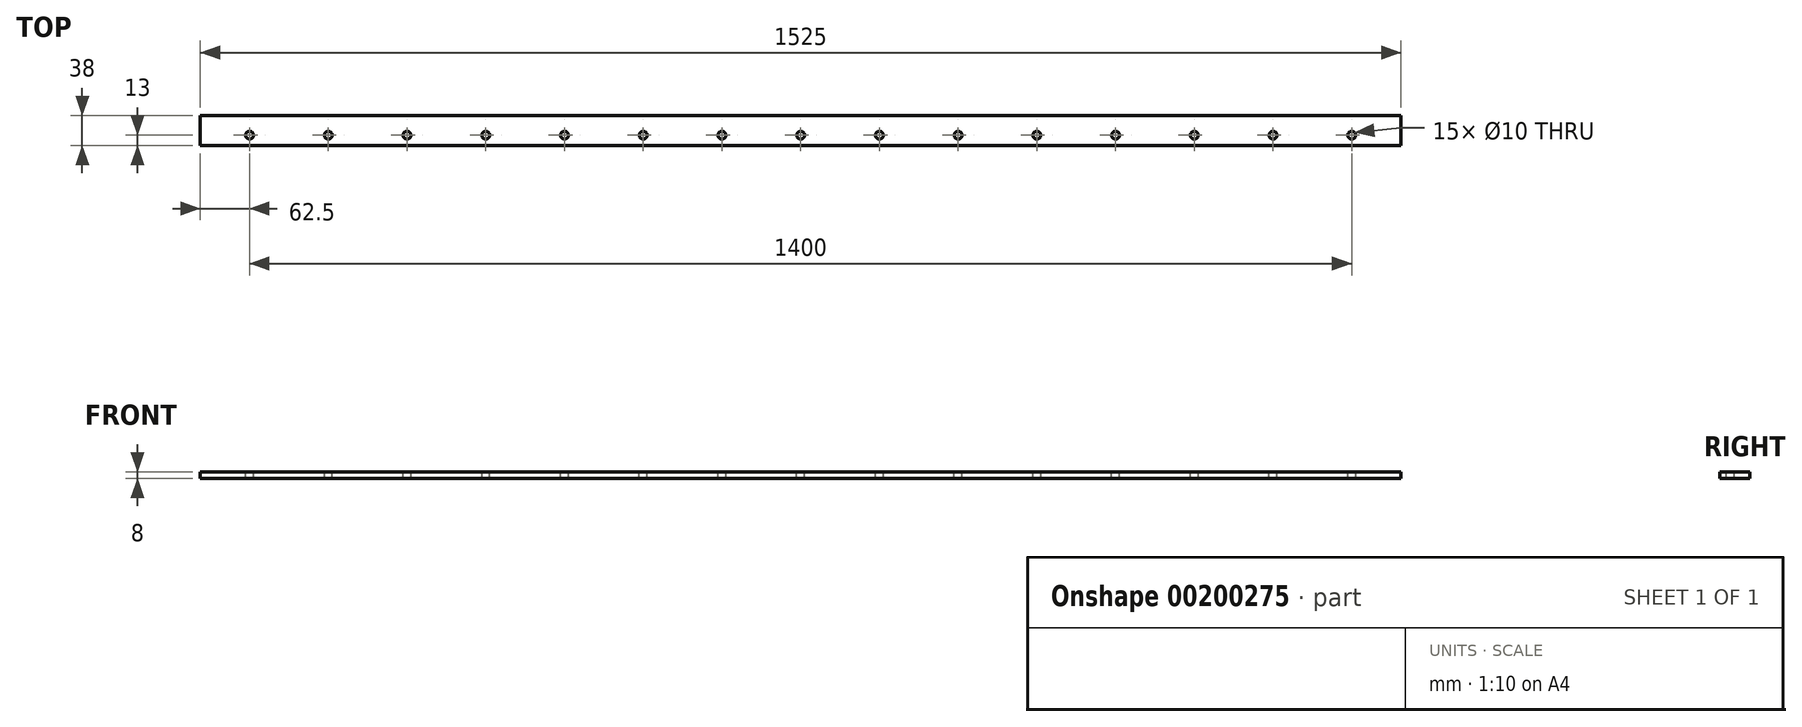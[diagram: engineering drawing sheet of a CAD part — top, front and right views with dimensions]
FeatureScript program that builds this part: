
annotation { "Feature Type Name" : "Feature", "Feature Type Description" : "" }
export const myFeature = defineFeature(function(context is Context, id is Id, definition is map)
    precondition{}
    {
        {
            var Q0;
            Q0=qCreatedBy(makeId("Top.planeOp"),FACE);
            var sketch = newSketch(context, id + "F0", { "sketchPlane" : qUnion([Q0])});
            skLineSegment(sketch, "E0.bottom", {"start": v(762.5, -19) * mm, "end": v(-762.5, -19) * mm});
            skLineSegment(sketch, "E0.top", {"start": v(762.5, 19) * mm, "end": v(-762.5, 19) * mm});
            skLineSegment(sketch, "E0.left", {"start": v(762.5, -19) * mm, "end": v(762.5, 19) * mm});
            skLineSegment(sketch, "E0.right", {"start": v(-762.5, -19) * mm, "end": v(-762.5, 19) * mm});
            skPoint(sketch, "E0.middle", {"position": v(0, 0) * mm});
            skSolve(sketch);
        }
        {
            var Q0;
            Q0 = qSketchRegion(id + "F0", true);
            extrude(context, id + "F1", {"entities" : qUnion([Q0]), "depth" : 8 * mm});
        }
        {
            var Q0;
            Q0=makeQuery(id+"F1.opExtrude","CAP_FACE",FACE,{"disambiguationData":[OSD([sQuery(id+"F0.wireOp",EDGE,"E0.bottom"),sQuery(id+"F0.wireOp",EDGE,"E0.top"),sQuery(id+"F0.wireOp",EDGE,"E0.left"),sQuery(id+"F0.wireOp",EDGE,"E0.right")])],"isStart":false});
            var sketch = newSketch(context, id + "F2", { "sketchPlane" : qUnion([Q0])});
            skCircle(sketch, "E1", {"center": v(-700, -6) * mm, "radius": 5 * mm});
            skCircle(sketch, "E2.1.0.0", {"center": v(-600, -6) * mm, "radius": 5 * mm});
            skCircle(sketch, "E2.2.0.0", {"center": v(-500, -6) * mm, "radius": 5 * mm});
            skCircle(sketch, "E2.3.0.0", {"center": v(-400, -6) * mm, "radius": 5 * mm});
            skCircle(sketch, "E2.4.0.0", {"center": v(-300, -6) * mm, "radius": 5 * mm});
            skCircle(sketch, "E2.5.0.0", {"center": v(-200, -6) * mm, "radius": 5 * mm});
            skCircle(sketch, "E2.6.0.0", {"center": v(-100, -6) * mm, "radius": 5 * mm});
            skCircle(sketch, "E2.7.0.0", {"center": v(0, -6) * mm, "radius": 5 * mm});
            skCircle(sketch, "E2.8.0.0", {"center": v(100, -6) * mm, "radius": 5 * mm});
            skCircle(sketch, "E2.9.0.0", {"center": v(200, -6) * mm, "radius": 5 * mm});
            skCircle(sketch, "E2.10.0.0", {"center": v(300, -6) * mm, "radius": 5 * mm});
            skCircle(sketch, "E2.11.0.0", {"center": v(400, -6) * mm, "radius": 5 * mm});
            skCircle(sketch, "E2.12.0.0", {"center": v(500, -6) * mm, "radius": 5 * mm});
            skCircle(sketch, "E2.13.0.0", {"center": v(600, -6) * mm, "radius": 5 * mm});
            skCircle(sketch, "E2.14.0.0", {"center": v(700, -6) * mm, "radius": 5 * mm});
            skLineSegment(sketch, "E2.direction1", {"start": v(-700, -6) * mm, "end": v(-600, -6) * mm, "construction": true});
            skLineSegment(sketch, "E3", {"start": v(0, 19) * mm, "end": v(0, -19) * mm, "construction": true});
            skSolve(sketch);
        }
        {
            var Q0;
            Q0 = qSketchRegion(id + "F2", true);
            extrude(context, id + "F3", {"entities" : qUnion([Q0]), "operationType" : NewBodyOperationType.REMOVE, "endBound" : BoundingType.THROUGH_ALL, "oppositeDirection" : true, "depth" : 25 * mm});
        }
    });
